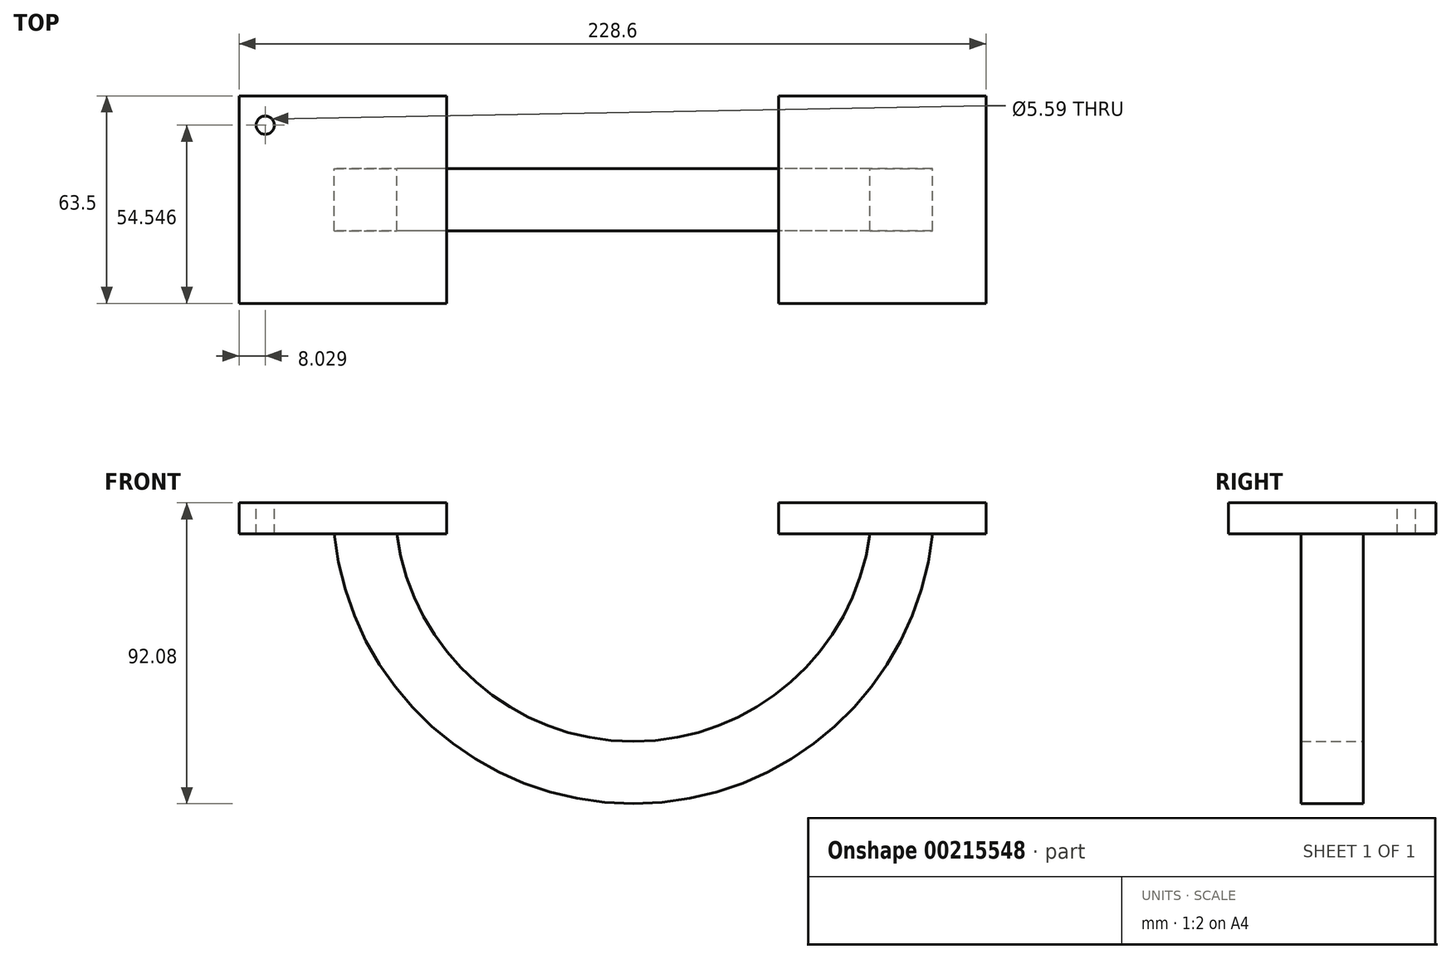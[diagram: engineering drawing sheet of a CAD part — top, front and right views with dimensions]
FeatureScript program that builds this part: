
annotation { "Feature Type Name" : "Feature", "Feature Type Description" : "" }
export const myFeature = defineFeature(function(context is Context, id is Id, definition is map)
    precondition{}
    {
        {
            var Q0;
            Q0=qCreatedBy(makeId("Top.planeOp"),FACE);
            var sketch = newSketch(context, id + "F0", { "sketchPlane" : qUnion([Q0])});
            skLineSegment(sketch, "E0.bottom", {"start": v(-57.17, -31.75) * mm, "end": v(-120.67, -31.75) * mm});
            skLineSegment(sketch, "E0.top", {"start": v(-57.17, 31.75) * mm, "end": v(-120.67, 31.75) * mm});
            skLineSegment(sketch, "E0.left", {"start": v(-57.17, -31.75) * mm, "end": v(-57.17, 31.75) * mm});
            skLineSegment(sketch, "E0.right", {"start": v(-120.67, -31.75) * mm, "end": v(-120.67, 31.75) * mm});
            skPoint(sketch, "E0.middle", {"position": v(-88.92, 0) * mm});
            skLineSegment(sketch, "E1.bottom", {"start": v(107.93, -31.75) * mm, "end": v(44.43, -31.75) * mm});
            skLineSegment(sketch, "E1.top", {"start": v(107.93, 31.75) * mm, "end": v(44.43, 31.75) * mm});
            skLineSegment(sketch, "E1.left", {"start": v(107.93, -31.75) * mm, "end": v(107.93, 31.75) * mm});
            skLineSegment(sketch, "E1.right", {"start": v(44.43, -31.75) * mm, "end": v(44.43, 31.75) * mm});
            skPoint(sketch, "E1.middle", {"position": v(76.18, 0) * mm});
            skCircle(sketch, "E2", {"center": v(-112.64, 22.8) * mm, "radius": 2.8 * mm});
            skSolve(sketch);
        }
        {
            var Q0;
            Q0=qCreatedBy(makeId("Top.planeOp"),FACE);
            var sketch = newSketch(context, id + "F1", { "sketchPlane" : qUnion([Q0])});
            skLineSegment(sketch, "E3.bottom", {"start": v(-73.03, -9.52) * mm, "end": v(-92.08, -9.52) * mm});
            skLineSegment(sketch, "E3.top", {"start": v(-73.03, 9.53) * mm, "end": v(-92.08, 9.53) * mm});
            skLineSegment(sketch, "E3.left", {"start": v(-73.03, -9.52) * mm, "end": v(-73.03, 9.53) * mm});
            skLineSegment(sketch, "E3.right", {"start": v(-92.08, -9.52) * mm, "end": v(-92.08, 9.53) * mm});
            skPoint(sketch, "E3.middle", {"position": v(-82.55, 0) * mm});
            skPoint(sketch, "E4.startSnap0", {"position": v(-82.55, -9.52) * mm});
            skLineSegment(sketch, "E5", {"start": v(0, 9.53) * mm, "end": v(0, -9.52) * mm, "construction": true});
            skSolve(sketch);
        }
        {
            var Q0;
            Q0=makeQuery(id+"F1.imprint","IMPRINT",FACE,{"disambiguationData":[TD([[makeQuery(id+"F1.imprint","IMPRINT",EDGE,{"derivedFrom":sQuery(id+"F1.wireOp",EDGE,"E3.bottom")}),-1.0]])]});
            var Q1;
            Q1=sQuery(id+"F1.wireOp",EDGE,"E5");
            revolve(context, id + "F2", {"entities" : qUnion([Q0]), "axis" : qUnion([Q1]), "revolveType" : RevolveType.ONE_DIRECTION, "angle" : 180 * degree});
        }
        {
            var Q0;
            Q0=makeQuery(id+"F0.imprint","IMPRINT",FACE,{"disambiguationData":[TD([[makeQuery(id+"F0.imprint","IMPRINT",EDGE,{"derivedFrom":sQuery(id+"F0.wireOp",EDGE,"E0.bottom")}),-1.0]])]});
            extrude(context, id + "F3", {"entities" : qUnion([Q0]), "operationType" : NewBodyOperationType.ADD, "oppositeDirection" : true, "depth" : 9.52 * mm});
        }
        {
            var Q0;
            Q0=makeQuery(id+"F0.imprint","IMPRINT",FACE,{"disambiguationData":[TD([[makeQuery(id+"F0.imprint","IMPRINT",EDGE,{"derivedFrom":sQuery(id+"F0.wireOp",EDGE,"E1.bottom")}),-1.0]])]});
            var Q1;
            Q1 = qSketchRegion(id + "F1", true);
            extrude(context, id + "F4", {"entities" : qUnion([Q0, Q1]), "operationType" : NewBodyOperationType.ADD, "oppositeDirection" : true, "depth" : 9.52 * mm});
        }
    });
